# Revit family: Seat-WCSeatCover-Vitra-MemoriaSeries_106
name_source: partatom
category: Plumbing Fixtures
revit_build: Autodesk Revit 2017 (Build: 20160225_1515(x64)
units: mm (PartAtom-declared; Revit-internal decimal feet)

## family parameters
Cut with Voids When Loaded = No
Host = Face
OmniClass Number = 23.45.00.00
OmniClass Title = Sanitary, Laundry, and Cleaning Equipment
Part Type = Normal
Room Calculation Point = No
Round Connector Dimension = Use Diameter
Shared = Yes

## types (12) — shared parameters
BIMobject category = Sanitary - Toilet Seats
Brand = VitrA
CW Connection = No
Default Elevation = 410 mm  [stored 1.34514 ft]
Design country = Turkey
HW Connection = No
IFC Classification = Sanitary Terminal
Main Material = Duroplast
Manufacturer = Vitra
Manufacturer name = Vitra
NBS Referans Code = 35-93-95
NBS Referans Description = Wc Seats And Covers
Nominal Depth (mm) = 465 mm  [stored 1.52559 ft]
Nominal Height (mm) = 70 mm
Nominal Width (mm) = 420 mm  [stored 1.37795 ft]
OmniClass Code = 23-31 19 19 11
OmniClass Description = Toilets
Product certification = https://www.vitraglobal.com
Product family = Memoria
Product group = Memoria WC Seat
UNSPSC Code = 35-93-95
UNSPSC Description = Water Operated Water Closets
URL = https://www.vitra.com.tr
Uniclass 1.4 Code = L72164
Uniclass 1.4 Description = Toilets
Uniclass 2.0 Code = PR-35-93-95
Uniclass 2.0 Description = Wc Seats And Covers
Uniclass 2015 Code = Pr_40_20_93_95
Uniclass 2015 Name = WC seats and covers
Vent Connection = No
Warranty Period (Year) = 2 Years
Waste Connection = No
Weight Net (kg) = 3.3
Youtube = https://www.youtube.com

## per-type parameters (varying)
| type | Article No. (default) | Color | Description | Model | Primary Material | Product SKU | Product url | Technical description |
| Seat-WCSeat, Metal hinge, top fixing-106-001-009 | 106-001-009 | Matte White | VitrA Memoria WC Seat - Metal Hinge - Top Fixing | 106-001-009 | MatteWhite-WCSeat | 106-001-009 | https://www.vitraglobal.com | https://www.vitraglobal.com |
| Seat-WCSeat, Metal hinge, top fixing-106-003-009 | 106-003-009 | White | VitrA Memoria WC Seat - Metal Hinge - Top Fixing | 106-003-009 | White-WCSeat | 106-003-009 | https://www.vitraglobal.com | https://www.vitraglobal.com |
| Seat-WCSeat, Metal hinge, top fixing-106-020-009 | 106-020-009 | Matte Taupe | VitrA Memoria WC Seat - Metal Hinge - Top Fixing | 106-020-009 | MatteTaupe-WCSeat | 106-020-009 | https://www.vitraglobal.com | https://www.vitraglobal.com |
| Seat-WCSeat, Metal hinge, top fixing-106-083-009 | 106-083-009 | Matte Black | VitrA Memoria WC Seat - Metal Hinge - Top Fixing | 106-083-009 | MatteBlack-WCSeat | 106-083-009 | https://www.vitraglobal.com | https://www.vitraglobal.com |
| Seat-WCSeat, Metal hinge, Quick Release, top fixing-106-001R009 | 106-001R009 | Matte White | VitrA Memoria WC Seat - Metal Hinge - Quick Release - Top Fixing | 106-001R009 | MatteWhite-WCSeat | 106-001R009 | https://www.vitraglobal.com | https://www.vitraglobal.com |
| Seat-WCSeat, Metal hinge, Quick Release, top fixing-106-003R009 | 106-003R009 | White | VitrA Memoria WC Seat - Metal Hinge - Quick Release - Top Fixing | 106-003R009 | White-WCSeat | 106-003R009 | https://www.vitraglobal.com | https://www.vitraglobal.com |
| Seat-WCSeat, Metal hinge, Quick Release, top fixing-106-020R009 | 106-020R009 | Matte Taupe | VitrA Memoria WC Seat - Metal Hinge - Quick Release - Top Fixing | 106-020R009 | MatteTaupe-WCSeat | 106-020R009 | https://www.vitraglobal.com | https://www.vitraglobal.com |
| Seat-WCSeat, Metal hinge, Quick Release, top fixing-106-083R009 | 106-083R009 | Matte Black | VitrA Memoria WC Seat - Metal Hinge - Quick Release - Top Fixing | 106-083R009 | MatteBlack-WCSeat | 106-083R009 | https://www.vitraglobal.com | https://www.vitraglobal.com |
| Seat-WCSeat, Metal hinge, Quick Release, top fixing-106-001H209 | 106-001H209 | Matte White | VitrA Memoria WC Seat - Metal Hinge - Quick Release - Top Fixing | 106-001H209 | MatteWhite-WCSeat | 106-001H209 | https://www.vitra-india.com | https://www.vitra-india.com |
| Seat-WCSeat, Metal hinge, Quick Release, top fixing-106-003H209 | 106-003H209 | White | VitrA Memoria WC Seat - Metal Hinge - Quick Release - Top Fixing | 106-003H209 | White-WCSeat | 106-003H209 | https://www.vitra-india.com | https://www.vitra-india.com |
| Seat-WCSeat, Metal hinge, Quick Release, top fixing-106-020H209 | 106-020H209 | Matte Taupe | VitrA Memoria WC Seat - Metal Hinge - Quick Release - Top Fixing | 106-020H209 | MatteTaupe-WCSeat | 106-020H209 | https://www.vitra-india.com | https://www.vitra-india.com |
| Seat-WCSeat, Metal hinge, Quick Release, top fixing-106-083H209 | 106-083H209 | Matte Black | VitrA Memoria WC Seat - Metal Hinge - Quick Release - Top Fixing | 106-083H209 | MatteBlack-WCSeat | 106-083H209 | https://www.vitra-india.com | https://www.vitra-india.com |

note: [stored X ft] marks values corroborated as IEEE doubles in the binary element streams (Revit-internal decimal feet)

## geometry (parser evidence)
native form markers: Sweep x2
no freeform markers — native parametric forms only
